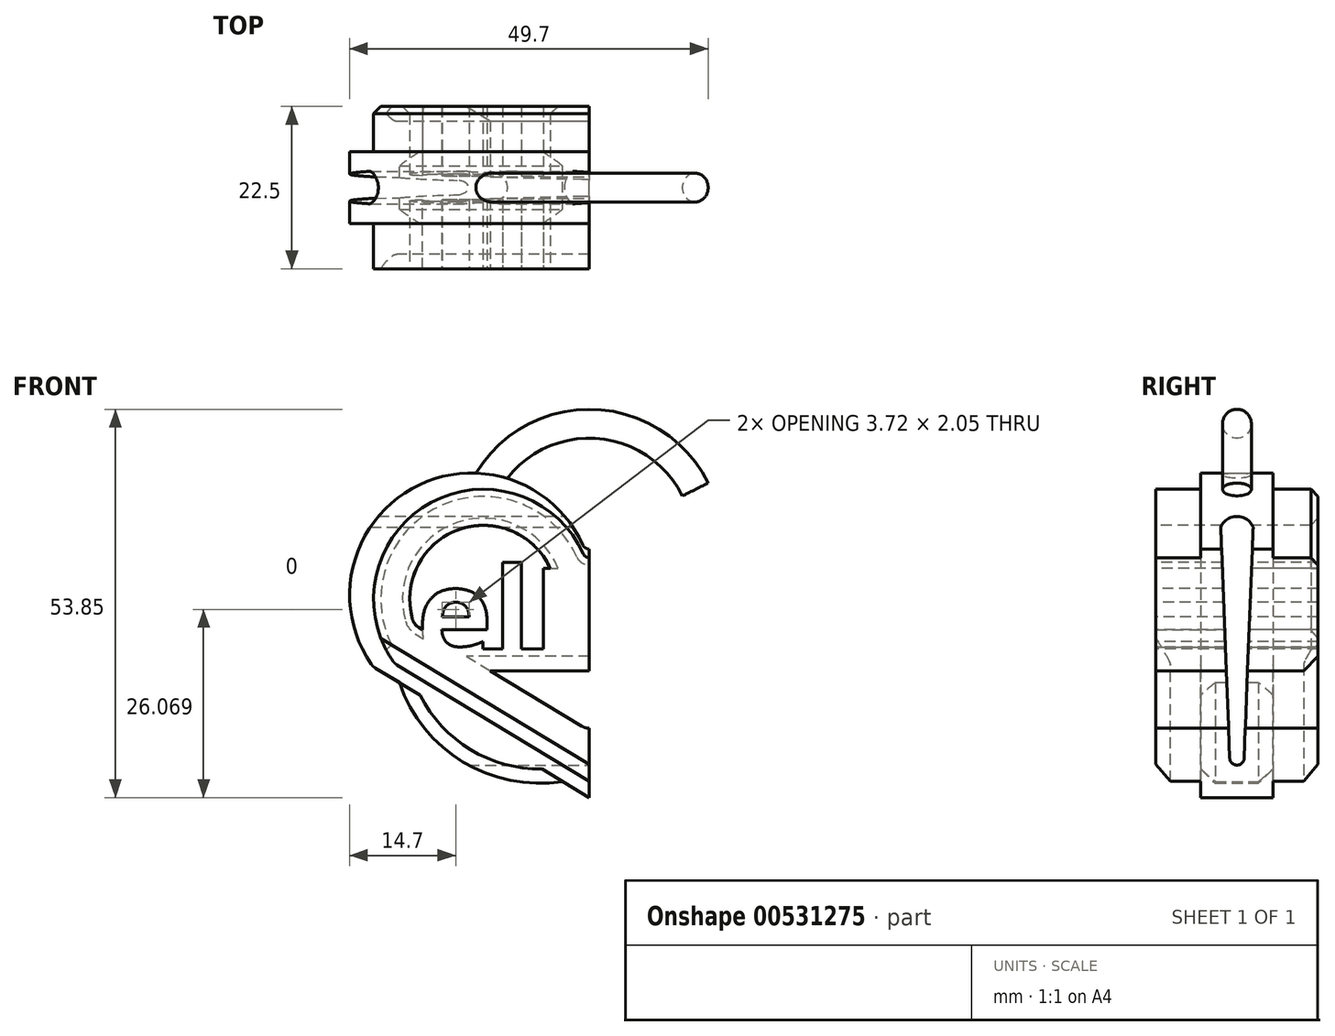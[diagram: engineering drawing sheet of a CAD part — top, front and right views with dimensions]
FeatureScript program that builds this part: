
annotation { "Feature Type Name" : "Feature", "Feature Type Description" : "" }
export const myFeature = defineFeature(function(context is Context, id is Id, definition is map)
    precondition{}
    {
        {
            var Q0;
            Q0=qCreatedBy(makeId("Front.planeOp"),FACE);
            var sketch = newSketch(context, id + "F0", { "sketchPlane" : qUnion([Q0])});
            skLineSegment(sketch, "E0", {"start": v(0, 22.5) * mm, "end": v(0, -22.5) * mm});
            skArc(sketch, "E1", {"start": v(-0.91, 12.55) * mm, "mid": v(-24.6, 20.33) * mm, "end": v(-30.26, -3.96) * mm});
            skPoint(sketch, "E2", {"position": v(-16.32, 22.5) * mm});
            skLineSegment(sketch, "E3", {"start": v(-29.64, -4.54) * mm, "end": v(0, -22.5) * mm});
            skLineSegment(sketch, "E4", {"start": v(0, 0) * mm, "end": v(-45, 0) * mm, "construction": true});
            skPoint(sketch, "E5", {"position": v(-22.5, 0) * mm});
            skArc(sketch, "E6", {"start": v(-26.32, -6.55) * mm, "mid": v(-17.5, -17.55) * mm, "end": v(-3.68, -20.27) * mm});
            skLineSegment(sketch, "E7.MirrorCS", {"start": v(29.64, -4.54) * mm, "end": v(0, -22.5) * mm});
            skArc(sketch, "E8.MirrorCS", {"start": v(26.32, -6.55) * mm, "mid": v(17.5, -17.55) * mm, "end": v(3.68, -20.27) * mm});
            skPoint(sketch, "E9.MirrorP", {"position": v(22.5, 0) * mm});
            skArc(sketch, "E10.MirrorCS", {"start": v(0.91, 12.55) * mm, "mid": v(24.6, 20.33) * mm, "end": v(30.26, -3.96) * mm});
            skPoint(sketch, "E11.visualSharp", {"position": v(0, 10) * mm});
            skArc(sketch, "E11.filletArc", {"start": v(-0.91, 12.55) * mm, "mid": v(0, 11.96) * mm, "end": v(0.91, 12.55) * mm});
            skPoint(sketch, "E12.visualSharp", {"position": v(-30, -4.32) * mm});
            skArc(sketch, "E12.filletArc", {"start": v(-30.26, -3.96) * mm, "mid": v(-29.98, -4.28) * mm, "end": v(-29.64, -4.54) * mm});
            skPoint(sketch, "E13.visualSharp", {"position": v(30, -4.32) * mm});
            skArc(sketch, "E13.filletArc", {"start": v(29.64, -4.54) * mm, "mid": v(29.98, -4.28) * mm, "end": v(30.26, -3.96) * mm});
            skSolve(sketch);
        }
        {
            var Q0;
            {var subQ0=sQuery(id+"F0.wireOp",EDGE,"E6");Q0=makeQuery(id+"F0.imprint","IMPRINT",FACE,{"disambiguationData":[TD([[makeQuery(id+"F0.imprint","IMPRINT",EDGE,{"derivedFrom":subQ0}),1.0]])]});}
            var Q1;
            {var subQ5=sQuery(id+"F0.wireOp",EDGE,"E1");Q1=makeQuery(id+"F0.imprint","IMPRINT",FACE,{"disambiguationData":[TD([[makeQuery(id+"F0.imprint","IMPRINT",EDGE,{"derivedFrom":subQ5}),1.0]])]});}
            var Q2;
            {var subQ9=sQuery(id+"F0.wireOp",EDGE,"E10.MirrorCS");Q2=makeQuery(id+"F0.imprint","IMPRINT",FACE,{"disambiguationData":[TD([[makeQuery(id+"F0.imprint","IMPRINT",EDGE,{"derivedFrom":subQ9}),-1.0]])]});}
            var Q3;
            {var subQ0=sQuery(id+"F0.wireOp",EDGE,"E8.MirrorCS");Q3=makeQuery(id+"F0.imprint","IMPRINT",FACE,{"disambiguationData":[TD([[makeQuery(id+"F0.imprint","IMPRINT",EDGE,{"derivedFrom":subQ0}),-1.0]])]});}
            extrude(context, id + "F1", {"entities" : qUnion([Q0, Q1, Q2, Q3]), "endBound" : BoundingType.SYMMETRIC, "depth" : 10 * mm, "offsetDistance" : 25 * mm});
        }
        {
            var Q0;
            {var subQ5=sQuery(id+"F0.wireOp",EDGE,"E1");Q0=makeQuery(id+"F0.imprint","IMPRINT",FACE,{"disambiguationData":[TD([[makeQuery(id+"F0.imprint","IMPRINT",EDGE,{"derivedFrom":subQ5}),1.0]])]});}
            var Q1;
            {var subQ9=sQuery(id+"F0.wireOp",EDGE,"E10.MirrorCS");Q1=makeQuery(id+"F0.imprint","IMPRINT",FACE,{"disambiguationData":[TD([[makeQuery(id+"F0.imprint","IMPRINT",EDGE,{"derivedFrom":subQ9}),-1.0]])]});}
            extrude(context, id + "F2", {"entities" : qUnion([Q0, Q1]), "endBound" : BoundingType.SYMMETRIC, "depth" : 25 * mm, "offsetDistance" : 25 * mm});
        }
        {
            var Q0;
            Q0=makeQuery(id+"F2.opExtrude","SWEPT_BODY",BODY,{"disambiguationData":[OSD([sQuery(id+"F0.wireOp",EDGE,"E1"),sQuery(id+"F0.wireOp",EDGE,"E3"),sQuery(id+"F0.wireOp",EDGE,"E7.MirrorCS"),sQuery(id+"F0.wireOp",EDGE,"E10.MirrorCS"),sQuery(id+"F0.wireOp",EDGE,"E11.filletArc"),sQuery(id+"F0.wireOp",EDGE,"E12.filletArc"),sQuery(id+"F0.wireOp",EDGE,"E13.filletArc")])]});
            var Q1;
            Q1=qCreatedBy(makeId("Origin.pointOp"),VERTEX);
            transform(context, id + "F3", {"entities" : qUnion([Q0]), "transformType" : TransformType.SCALE_UNIFORMLY, "scale" : .9, "scalePoint" : qUnion([Q1]), "makeCopy" : false});
        }
        {
            var Q0;
            Q0=makeQuery(id+"F1.opExtrude","CAP_EDGE",EDGE,{"disambiguationData":[OSD([sQuery(id+"F0.wireOp",EDGE,"E8.MirrorCS")])],"isStart":false});
            var Q1;
            Q1=makeQuery(id+"F1.opExtrude","CAP_EDGE",EDGE,{"disambiguationData":[OSD([sQuery(id+"F0.wireOp",EDGE,"E8.MirrorCS")])],"isStart":true});
            var Q2;
            Q2=makeQuery(id+"F2.opExtrude","CAP_EDGE",EDGE,{"disambiguationData":[OSD([sQuery(id+"F0.wireOp",EDGE,"E7.MirrorCS")])],"isStart":false});
            var Q3;
            Q3=makeQuery(id+"F2.opExtrude","CAP_EDGE",EDGE,{"disambiguationData":[OSD([sQuery(id+"F0.wireOp",EDGE,"E13.filletArc")])],"isStart":false});
            var Q4;
            Q4=makeQuery(id+"F2.opExtrude","CAP_EDGE",EDGE,{"disambiguationData":[OSD([sQuery(id+"F0.wireOp",EDGE,"E7.MirrorCS")])],"isStart":true});
            var Q5;
            Q5=makeQuery(id+"F2.opExtrude","CAP_EDGE",EDGE,{"disambiguationData":[OSD([sQuery(id+"F0.wireOp",EDGE,"E3")])],"isStart":false});
            var Q6;
            Q6=makeQuery(id+"F1.opExtrude","CAP_EDGE",EDGE,{"disambiguationData":[OSD([sQuery(id+"F0.wireOp",EDGE,"E6")])],"isStart":false});
            var Q7;
            Q7=makeQuery(id+"F1.opExtrude","CAP_EDGE",EDGE,{"disambiguationData":[OSD([sQuery(id+"F0.wireOp",EDGE,"E6")])],"isStart":true});
            var Q8;
            Q8=makeQuery(id+"F2.opExtrude","CAP_EDGE",EDGE,{"disambiguationData":[OSD([sQuery(id+"F0.wireOp",EDGE,"E3")])],"isStart":true});
            chamfer(context, id + "F4", {"entities" : qUnion([Q0, Q1, Q2, Q3, Q4, Q5, Q6, Q7, Q8]), "width" : 2 * mm});
        }
        {
            var Q0;
            Q0=makeQuery(id+"F1.opExtrude","SWEPT_FACE",FACE,{"disambiguationData":[OSD([sQuery(id+"F0.wireOp",EDGE,"E10.MirrorCS")])]});
            var Q1;
            Q1=makeQuery(id+"F2.opExtrude","CAP_EDGE",EDGE,{"disambiguationData":[OSD([sQuery(id+"F0.wireOp",EDGE,"E1")])],"isStart":true});
            var Q2;
            Q2=makeQuery(id+"F2.opExtrude","CAP_EDGE",EDGE,{"disambiguationData":[OSD([sQuery(id+"F0.wireOp",EDGE,"E10.MirrorCS")])],"isStart":false});
            chamfer(context, id + "F5", {"entities" : qUnion([Q0, Q1, Q2]), "width" : 1 * mm, "tangentPropagation" : true});
        }
        {
            var Q0;
            Q0=qCreatedBy(makeId("Right.planeOp"),FACE);
            var sketch = newSketch(context, id + "F6", { "sketchPlane" : qUnion([Q0])});
            skLineSegment(sketch, "E14", {"start": v(15, 15) * mm, "end": v(-15, 15) * mm, "construction": true});
            skLineSegment(sketch, "E15", {"start": v(-4, 22.5) * mm, "end": v(4, 22.5) * mm, "construction": true});
            skLineSegment(sketch, "E16.0", {"start": v(-5, -22.5) * mm, "end": v(5, -22.5) * mm, "construction": true});
            skLineSegment(sketch, "E17.0", {"start": v(11.25, -17.91) * mm, "end": v(11.25, -1.3) * mm, "construction": true});
            skLineSegment(sketch, "E18.0", {"start": v(11.25, -1.3) * mm, "end": v(11.25, 19.25) * mm, "construction": true});
            skLineSegment(sketch, "E19.0", {"start": v(-11.25, 19.25) * mm, "end": v(-11.25, -1.3) * mm, "construction": true});
            skLineSegment(sketch, "E20.0", {"start": v(-11.25, -1.3) * mm, "end": v(-11.25, -17.91) * mm, "construction": true});
            skLineSegment(sketch, "E21.0", {"start": v(-3, -6.55) * mm, "end": v(3, -6.55) * mm, "construction": true});
            skArc(sketch, "E22", {"start": v(2.25, 15) * mm, "mid": v(0, 16.5) * mm, "end": v(-2.25, 15) * mm});
            skPoint(sketch, "E23", {"position": v(0, 16.5) * mm});
            skPoint(sketch, "E24", {"position": v(0, 22.5) * mm});
            skPoint(sketch, "E25", {"position": v(0, 15) * mm});
            skLineSegment(sketch, "E26", {"start": v(15, -42.64) * mm, "end": v(-15, -42.64) * mm, "construction": true});
            skPoint(sketch, "E27", {"position": v(0, -42.64) * mm});
            skLineSegment(sketch, "E28", {"start": v(2.25, 15) * mm, "end": v(1, -17.04) * mm});
            skLineSegment(sketch, "E29", {"start": v(-2.25, 15) * mm, "end": v(-1, -17.04) * mm});
            skArc(sketch, "E30.filletArc", {"start": v(-1, -17.04) * mm, "mid": v(0, -18) * mm, "end": v(1, -17.04) * mm});
            skSolve(sketch);
        }
        {
            var Q0;
            Q0 = qSketchRegion(id + "F6", true);
            extrude(context, id + "F7", {"entities" : qUnion([Q0]), "operationType" : NewBodyOperationType.REMOVE, "endBound" : BoundingType.SYMMETRIC, "oppositeDirection" : true, "depth" : 70 * mm, "offsetDistance" : 25 * mm, "hasSecondDirection" : true, "secondDirectionBound" : SecondDirectionBoundingType.THROUGH_ALL, "secondDirectionOppositeDirection" : true, "secondDirectionDepth" : 25 * mm});
        }
        {
            var Q0;
            Q0=makeQuery(id+"F2.opExtrude","CAP_FACE",FACE,{"disambiguationData":[OSD([sQuery(id+"F0.wireOp",EDGE,"E1"),sQuery(id+"F0.wireOp",EDGE,"E3"),sQuery(id+"F0.wireOp",EDGE,"E7.MirrorCS"),sQuery(id+"F0.wireOp",EDGE,"E10.MirrorCS"),sQuery(id+"F0.wireOp",EDGE,"E11.filletArc"),sQuery(id+"F0.wireOp",EDGE,"E12.filletArc"),sQuery(id+"F0.wireOp",EDGE,"E13.filletArc")])],"isStart":false});
            var sketch = newSketch(context, id + "F8", { "sketchPlane" : qUnion([Q0])});
            skArc(sketch, "E31.0", {"start": v(-5.38, 9.24) * mm, "mid": v(-18.2, 14.63) * mm, "end": v(-24.5, 2.24) * mm});
            skArc(sketch, "E31.1", {"start": v(5.38, 9.24) * mm, "mid": v(0, 5.76) * mm, "end": v(-5.38, 9.24) * mm});
            skLineSegment(sketch, "E31.2", {"start": v(-23.62, 1.08) * mm, "end": v(-1.04, -12.6) * mm});
            skLineSegment(sketch, "E31.3", {"start": v(1.04, -12.6) * mm, "end": v(23.62, 1.08) * mm});
            skArc(sketch, "E31.4", {"start": v(24.5, 2.24) * mm, "mid": v(18.2, 14.63) * mm, "end": v(5.38, 9.24) * mm});
            skPoint(sketch, "E32.visualSharp", {"position": v(0, -13.23) * mm});
            skArc(sketch, "E32.filletArc", {"start": v(-1.04, -12.6) * mm, "mid": v(0, -12.9) * mm, "end": v(1.04, -12.6) * mm});
            skPoint(sketch, "E33.visualSharp", {"position": v(-24.25, 1.46) * mm});
            skArc(sketch, "E33.filletArc", {"start": v(-24.5, 2.24) * mm, "mid": v(-24.17, 1.58) * mm, "end": v(-23.62, 1.08) * mm});
            skPoint(sketch, "E34.visualSharp", {"position": v(24.25, 1.46) * mm});
            skArc(sketch, "E34.filletArc", {"start": v(23.62, 1.08) * mm, "mid": v(24.17, 1.58) * mm, "end": v(24.5, 2.24) * mm});
            skText(sketch, "E35", { "text": "elLex", "fontName": "OpenSans-Bold.ttf"});
            skLineSegment(sketch, "E36.bottom", {"start": v(-23.92, -1.91) * mm, "end": v(23.92, -1.91) * mm});
            skLineSegment(sketch, "E36.top", {"start": v(-21.45, -4.91) * mm, "end": v(21.45, -4.91) * mm});
            skLineSegment(sketch, "E36.left", {"start": v(-23.92, -1.91) * mm, "end": v(-23.92, -3.41) * mm});
            skLineSegment(sketch, "E36.right", {"start": v(23.92, -1.91) * mm, "end": v(23.92, -3.41) * mm});
            skLineSegment(sketch, "E37.0", {"start": v(-27.4, -1.3) * mm, "end": v(0, -17.91) * mm, "construction": true});
            skLineSegment(sketch, "E38.0", {"start": v(0, -17.91) * mm, "end": v(27.4, -1.3) * mm, "construction": true});
            skPoint(sketch, "E39.orphan", {"position": v(-23.92, -4.91) * mm});
            skPoint(sketch, "E40.orphan", {"position": v(23.92, -4.91) * mm});
            skLineSegment(sketch, "E41.bottom", {"start": v(-23.05, 10.9) * mm, "end": v(-1.78, 10.9) * mm});
            skLineSegment(sketch, "E41.top", {"start": v(-23.92, 7.9) * mm, "end": v(23.92, 7.9) * mm});
            skLineSegment(sketch, "E41.left", {"start": v(-23.92, 9.4) * mm, "end": v(-23.92, 7.9) * mm});
            skLineSegment(sketch, "E41.right", {"start": v(23.92, 9.4) * mm, "end": v(23.92, 7.9) * mm});
            skArc(sketch, "E42.0", {"start": v(1.73, 10.88) * mm, "mid": v(0, 9.76) * mm, "end": v(-1.73, 10.88) * mm});
            skLineSegment(sketch, "E43", {"start": v(1.73, 10.9) * mm, "end": v(23.05, 10.9) * mm});
            skPoint(sketch, "E44.orphan", {"position": v(-23.92, 10.9) * mm});
            const initialGuessF8  = {"E35": [-0.02392, -0.00341, 1, 0, 0.0128]};
            skSetInitialGuess(sketch, initialGuessF8);
            skSolve(sketch);
        }
        {
            var Q0;
            {var subQ13=sQuery(id+"F8.wireOp",EDGE,"E31.4");Q0=makeQuery(id+"F8.imprint","IMPRINT",FACE,{"disambiguationData":[TD([[makeQuery(id+"F8.imprint","IMPRINT",EDGE,{"derivedFrom":subQ13}),1.0]])]});}
            var Q1;
            Q1=makeQuery(id+"F8.imprint","IMPRINT",FACE,{"disambiguationData":[TD([[makeQuery(id+"F8.imprint","IMPRINT",EDGE,{"derivedFrom":sQuery(id+"F8.wireOp",EDGE,"E35.sketch_text.stroke-30")}),1.0]])]});
            var Q2;
            Q2=makeQuery(id+"F8.imprint","IMPRINT",FACE,{"disambiguationData":[TD([[makeQuery(id+"F8.imprint","IMPRINT",EDGE,{"derivedFrom":sQuery(id+"F8.wireOp",EDGE,"E35.sketch_text.stroke-0")}),1.0]])]});
            var Q3;
            {var subQ4=sQuery(id+"F8.wireOp",EDGE,"E33.filletArc");Q3=makeQuery(id+"F8.imprint","IMPRINT",FACE,{"disambiguationData":[TD([[makeQuery(id+"F8.imprint","IMPRINT",EDGE,{"derivedFrom":subQ4}),1.0]])]});}
            var Q4;
            {var subQ0=sQuery(id+"F8.wireOp",EDGE,"E41.top");var subQ1=sQuery(id+"F8.wireOp",EDGE,"E35.sketch_text.stroke-23");var subQ2=makeQuery(id+"F8.imprint","INTERSECT",VERTEX,{"derivedFrom":[subQ1,subQ0]});Q4=makeQuery(id+"F8.imprint","IMPRINT",FACE,{"disambiguationData":[TD([[makeQuery(id+"F8.imprint","IMPRINT",EDGE,{"disambiguationData":[TD([[subQ2,-1.0]])],"derivedFrom":subQ1}),1.0]])]});}
            var Q5;
            {var subQ2=sQuery(id+"F8.wireOp",EDGE,"E34.filletArc");Q5=makeQuery(id+"F8.imprint","IMPRINT",FACE,{"disambiguationData":[TD([[makeQuery(id+"F8.imprint","IMPRINT",EDGE,{"derivedFrom":subQ2}),1.0]])]});}
            var Q6;
            {var subQ11=sQuery(id+"F8.wireOp",EDGE,"E35.sketch_text.stroke-22");Q6=makeQuery(id+"F8.imprint","IMPRINT",FACE,{"disambiguationData":[TD([[makeQuery(id+"F8.imprint","IMPRINT",EDGE,{"derivedFrom":subQ11}),1.0]])]});}
            var Q7;
            {var subQ0=sQuery(id+"F8.wireOp",EDGE,"E41.bottom");var subQ1=sQuery(id+"F8.wireOp",EDGE,"E31.0");var subQ2=makeQuery(id+"F8.imprint","INTERSECT",VERTEX,{"disambiguationData":[OD(0.0)],"derivedFrom":[subQ1,subQ0]});Q7=makeQuery(id+"F8.imprint","IMPRINT",FACE,{"disambiguationData":[TD([[makeQuery(id+"F8.imprint","IMPRINT",EDGE,{"disambiguationData":[TD([[subQ2,1.0]])],"derivedFrom":subQ1}),1.0]])]});}
            var Q8;
            {var subQ0=sQuery(id+"F8.wireOp",EDGE,"E43");var subQ1=sQuery(id+"F8.wireOp",EDGE,"E31.4");var subQ2=makeQuery(id+"F8.imprint","INTERSECT",VERTEX,{"disambiguationData":[OD(0.0)],"derivedFrom":[subQ1,subQ0]});Q8=makeQuery(id+"F8.imprint","IMPRINT",FACE,{"disambiguationData":[TD([[makeQuery(id+"F8.imprint","IMPRINT",EDGE,{"disambiguationData":[TD([[subQ2,-1.0]])],"derivedFrom":subQ1}),1.0]])]});}
            var Q9;
            {var subQ0=sQuery(id+"F8.wireOp",EDGE,"E36.bottom");var subQ1=sQuery(id+"F8.wireOp",EDGE,"E31.3");var subQ2=makeQuery(id+"F8.imprint","INTERSECT",VERTEX,{"derivedFrom":[subQ1,subQ0]});Q9=makeQuery(id+"F8.imprint","IMPRINT",FACE,{"disambiguationData":[TD([[makeQuery(id+"F8.imprint","IMPRINT",EDGE,{"disambiguationData":[TD([[subQ2,-1.0]])],"derivedFrom":subQ1}),1.0]])]});}
            var Q10;
            {var subQ0=sQuery(id+"F8.wireOp",EDGE,"E32.filletArc");Q10=makeQuery(id+"F8.imprint","IMPRINT",FACE,{"disambiguationData":[TD([[makeQuery(id+"F8.imprint","IMPRINT",EDGE,{"derivedFrom":subQ0}),1.0]])]});}
            extrude(context, id + "F9", {"entities" : qUnion([Q0, Q1, Q2, Q3, Q4, Q5, Q6, Q7, Q8, Q9, Q10]), "operationType" : NewBodyOperationType.REMOVE, "endBound" : BoundingType.THROUGH_ALL, "oppositeDirection" : true, "depth" : 25 * mm, "offsetDistance" : 25 * mm});
        }
        {
            var Q0;
            Q0=makeQuery(id+"F9.boolean.opBoolean","COPY",EDGE,{"derivedFrom":makeQuery(id+"F9.opExtrude","CAP_EDGE",EDGE,{"disambiguationData":[OSD([sQuery(id+"F8.wireOp",EDGE,"E36.top")])],"isStart":true})});
            var Q1;
            {var subQ0=sQuery(id+"F8.wireOp",EDGE,"E31.2");Q1=makeQuery(id+"F9.boolean.opBoolean","COPY",EDGE,{"derivedFrom":makeQuery(id+"F9.opExtrude","CAP_EDGE",EDGE,{"disambiguationData":[OSD([subQ0]),TDD([makeQuery(id+"F8.imprint","IMPRINT",EDGE,{"disambiguationData":[TD([[makeQuery(id+"F8.imprint","INTERSECT",VERTEX,{"derivedFrom":[subQ0,sQuery(id+"F8.wireOp",EDGE,"E32.filletArc")]}),1.0]])],"derivedFrom":subQ0})])],"isStart":true})});}
            var Q2;
            Q2=makeQuery(id+"F9.boolean.opBoolean","INTERSECT",EDGE,{"derivedFrom":[makeQuery(id+"F2.opExtrude","CAP_FACE",FACE,{"disambiguationData":[OSD([sQuery(id+"F0.wireOp",EDGE,"E1"),sQuery(id+"F0.wireOp",EDGE,"E3"),sQuery(id+"F0.wireOp",EDGE,"E7.MirrorCS"),sQuery(id+"F0.wireOp",EDGE,"E10.MirrorCS"),sQuery(id+"F0.wireOp",EDGE,"E11.filletArc"),sQuery(id+"F0.wireOp",EDGE,"E12.filletArc"),sQuery(id+"F0.wireOp",EDGE,"E13.filletArc")])],"isStart":true}),makeQuery(id+"F9.opExtrude","SWEPT_FACE",FACE,{"disambiguationData":[OSD([sQuery(id+"F8.wireOp",EDGE,"E36.top")])]})]});
            var Q3;
            {var subQ0=sQuery(id+"F8.wireOp",EDGE,"E31.3");Q3=makeQuery(id+"F9.boolean.opBoolean","INTERSECT",EDGE,{"derivedFrom":[makeQuery(id+"F2.opExtrude","CAP_FACE",FACE,{"disambiguationData":[OSD([sQuery(id+"F0.wireOp",EDGE,"E1"),sQuery(id+"F0.wireOp",EDGE,"E3"),sQuery(id+"F0.wireOp",EDGE,"E7.MirrorCS"),sQuery(id+"F0.wireOp",EDGE,"E10.MirrorCS"),sQuery(id+"F0.wireOp",EDGE,"E11.filletArc"),sQuery(id+"F0.wireOp",EDGE,"E12.filletArc"),sQuery(id+"F0.wireOp",EDGE,"E13.filletArc")])],"isStart":true}),makeQuery(id+"F9.opExtrude","SWEPT_FACE",FACE,{"disambiguationData":[OSD([subQ0]),TDD([makeQuery(id+"F8.imprint","IMPRINT",EDGE,{"disambiguationData":[TD([[makeQuery(id+"F8.imprint","INTERSECT",VERTEX,{"derivedFrom":[subQ0,sQuery(id+"F8.wireOp",EDGE,"E32.filletArc")]}),-1.0]])],"derivedFrom":subQ0})])]})]});}
            chamfer(context, id + "F10", {"entities" : qUnion([Q0, Q1, Q2, Q3]), "width" : 2 * mm, "tangentPropagation" : true});
        }
        {
            var Q0;
            Q0=makeQuery(id+"F9.boolean.opBoolean","COPY",EDGE,{"derivedFrom":makeQuery(id+"F9.opExtrude","CAP_EDGE",EDGE,{"disambiguationData":[OSD([sQuery(id+"F8.wireOp",EDGE,"E31.0")])],"isStart":true})});
            var Q1;
            Q1=makeQuery(id+"F9.boolean.opBoolean","COPY",EDGE,{"derivedFrom":makeQuery(id+"F9.opExtrude","CAP_EDGE",EDGE,{"disambiguationData":[OSD([sQuery(id+"F8.wireOp",EDGE,"E31.4")])],"isStart":true})});
            var Q2;
            Q2=makeQuery(id+"F9.boolean.opBoolean","INTERSECT",EDGE,{"derivedFrom":[makeQuery(id+"F2.opExtrude","CAP_FACE",FACE,{"disambiguationData":[OSD([sQuery(id+"F0.wireOp",EDGE,"E1"),sQuery(id+"F0.wireOp",EDGE,"E3"),sQuery(id+"F0.wireOp",EDGE,"E7.MirrorCS"),sQuery(id+"F0.wireOp",EDGE,"E10.MirrorCS"),sQuery(id+"F0.wireOp",EDGE,"E11.filletArc"),sQuery(id+"F0.wireOp",EDGE,"E12.filletArc"),sQuery(id+"F0.wireOp",EDGE,"E13.filletArc")])],"isStart":true}),makeQuery(id+"F9.opExtrude","SWEPT_FACE",FACE,{"disambiguationData":[OSD([sQuery(id+"F8.wireOp",EDGE,"E31.1")])]})]});
            var Q3;
            Q3=makeQuery(id+"F9.boolean.opBoolean","INTERSECT",EDGE,{"derivedFrom":[makeQuery(id+"F2.opExtrude","CAP_FACE",FACE,{"disambiguationData":[OSD([sQuery(id+"F0.wireOp",EDGE,"E1"),sQuery(id+"F0.wireOp",EDGE,"E3"),sQuery(id+"F0.wireOp",EDGE,"E7.MirrorCS"),sQuery(id+"F0.wireOp",EDGE,"E10.MirrorCS"),sQuery(id+"F0.wireOp",EDGE,"E11.filletArc"),sQuery(id+"F0.wireOp",EDGE,"E12.filletArc"),sQuery(id+"F0.wireOp",EDGE,"E13.filletArc")])],"isStart":true}),makeQuery(id+"F9.opExtrude","SWEPT_FACE",FACE,{"disambiguationData":[OSD([sQuery(id+"F8.wireOp",EDGE,"E31.0")])]})]});
            var Q4;
            Q4=makeQuery(id+"F7.boolean.opBoolean","INTERSECT",EDGE,{"disambiguationData":[OD(1.0)],"derivedFrom":[makeQuery(id+"F1.opExtrude","SWEPT_FACE",FACE,{"disambiguationData":[OSD([sQuery(id+"F0.wireOp",EDGE,"E10.MirrorCS")])]}),makeQuery(id+"F7.opExtrude","SWEPT_FACE",FACE,{"disambiguationData":[OSD([sQuery(id+"F6.wireOp",EDGE,"E22")])]})]});
            var Q5;
            Q5=makeQuery(id+"F7.boolean.opBoolean","INTERSECT",EDGE,{"derivedFrom":[makeQuery(id+"F1.opExtrude","SWEPT_FACE",FACE,{"disambiguationData":[OSD([sQuery(id+"F0.wireOp",EDGE,"E8.MirrorCS")])]}),makeQuery(id+"F7.opExtrude","SWEPT_FACE",FACE,{"disambiguationData":[OSD([sQuery(id+"F6.wireOp",EDGE,"E30.filletArc")])]})]});
            var Q6;
            Q6=makeQuery(id+"F7.boolean.opBoolean","INTERSECT",EDGE,{"disambiguationData":[OD(1.0)],"derivedFrom":[makeQuery(id+"F1.opExtrude","SWEPT_FACE",FACE,{"disambiguationData":[OSD([sQuery(id+"F0.wireOp",EDGE,"E10.MirrorCS")])]}),makeQuery(id+"F7.opExtrude","SWEPT_FACE",FACE,{"disambiguationData":[OSD([sQuery(id+"F6.wireOp",EDGE,"E29")])]})]});
            var Q7;
            Q7=makeQuery(id+"F7.boolean.opBoolean","INTERSECT",EDGE,{"disambiguationData":[OD(1.0)],"derivedFrom":[makeQuery(id+"F1.opExtrude","SWEPT_FACE",FACE,{"disambiguationData":[OSD([sQuery(id+"F0.wireOp",EDGE,"E10.MirrorCS")])]}),makeQuery(id+"F7.opExtrude","SWEPT_FACE",FACE,{"disambiguationData":[OSD([sQuery(id+"F6.wireOp",EDGE,"E28")])]})]});
            var Q8;
            Q8=makeQuery(id+"F7.boolean.opBoolean","INTERSECT",EDGE,{"disambiguationData":[OD(1.0)],"derivedFrom":[makeQuery(id+"F1.opExtrude","SWEPT_FACE",FACE,{"disambiguationData":[OSD([sQuery(id+"F0.wireOp",EDGE,"E1")])]}),makeQuery(id+"F7.opExtrude","SWEPT_FACE",FACE,{"disambiguationData":[OSD([sQuery(id+"F6.wireOp",EDGE,"E22")])]})]});
            var Q9;
            Q9=makeQuery(id+"F7.boolean.opBoolean","INTERSECT",EDGE,{"derivedFrom":[makeQuery(id+"F1.opExtrude","SWEPT_FACE",FACE,{"disambiguationData":[OSD([sQuery(id+"F0.wireOp",EDGE,"E6")])]}),makeQuery(id+"F7.opExtrude","SWEPT_FACE",FACE,{"disambiguationData":[OSD([sQuery(id+"F6.wireOp",EDGE,"E30.filletArc")])]})]});
            var Q10;
            Q10=makeQuery(id+"F7.boolean.opBoolean","INTERSECT",EDGE,{"disambiguationData":[OD(1.0)],"derivedFrom":[makeQuery(id+"F1.opExtrude","SWEPT_FACE",FACE,{"disambiguationData":[OSD([sQuery(id+"F0.wireOp",EDGE,"E1")])]}),makeQuery(id+"F7.opExtrude","SWEPT_FACE",FACE,{"disambiguationData":[OSD([sQuery(id+"F6.wireOp",EDGE,"E28")])]})]});
            var Q11;
            Q11=makeQuery(id+"F7.boolean.opBoolean","INTERSECT",EDGE,{"disambiguationData":[OD(1.0)],"derivedFrom":[makeQuery(id+"F1.opExtrude","SWEPT_FACE",FACE,{"disambiguationData":[OSD([sQuery(id+"F0.wireOp",EDGE,"E1")])]}),makeQuery(id+"F7.opExtrude","SWEPT_FACE",FACE,{"disambiguationData":[OSD([sQuery(id+"F6.wireOp",EDGE,"E29")])]})]});
            chamfer(context, id + "F11", {"entities" : qUnion([Q0, Q1, Q2, Q3, Q4, Q5, Q6, Q7, Q8, Q9, Q10, Q11]), "width" : 1 * mm, "tangentPropagation" : true});
        }
        {
            var Q0;
            Q0=qCreatedBy(makeId("Front.planeOp"),FACE);
            var sketch = newSketch(context, id + "F12", { "sketchPlane" : qUnion([Q0])});
            skArc(sketch, "E45.0", {"start": v(-30.26, -3.96) * mm, "mid": v(-24.6, 20.33) * mm, "end": v(-0.91, 12.55) * mm, "construction": true});
            skArc(sketch, "E46.0", {"start": v(0.91, 12.55) * mm, "mid": v(24.6, 20.33) * mm, "end": v(30.26, -3.96) * mm, "construction": true});
            skArc(sketch, "E47.0", {"start": v(-0.91, 12.55) * mm, "mid": v(0, 11.96) * mm, "end": v(0.91, 12.55) * mm, "construction": true});
            skArc(sketch, "E48.0", {"start": v(-5.4, 9.28) * mm, "mid": v(-18.22, 14.62) * mm, "end": v(-24.5, 2.24) * mm, "construction": true});
            skArc(sketch, "E49.0", {"start": v(24.5, 2.24) * mm, "mid": v(18.2, 14.63) * mm, "end": v(5.38, 9.24) * mm, "construction": true});
            skArc(sketch, "E50", {"start": v(14.69, 20.23) * mm, "mid": v(0, 29.35) * mm, "end": v(-14.69, 20.23) * mm});
            skSolve(sketch);
        }
        {
            var Q0;
            Q0=sQuery(id+"F12.wireOp",EDGE,"E50");
            var Q1;
            Q1=sQuery(id+"F12.wireOp",VERTEX,"E50.end");
            cPlane(context, id + "F13", {"entities" : qUnion([Q0, Q1]), "cplaneType" : CPlaneType.CURVE_POINT, "offset" : 25 * mm, "width" : 150 * mm, "height" : 150 * mm});
        }
        {
            var Q0;
            Q0=qCreatedBy(id+"F13.planeOp",FACE);
            var sketch = newSketch(context, id + "F14", { "sketchPlane" : qUnion([Q0])});
            skCircle(sketch, "E51", {"center": v(-22.14, 0) * mm, "radius": 2 * mm});
            skSolve(sketch);
        }
        {
            var Q0;
            Q0=makeQuery(id+"F14.imprint","IMPRINT",FACE,{"disambiguationData":[TD([[makeQuery(id+"F14.imprint","IMPRINT",EDGE,{"derivedFrom":sQuery(id+"F14.wireOp",EDGE,"E51")}),1.0]])]});
            var Q1;
            Q1=sQuery(id+"F12.wireOp",EDGE,"E50");
            sweep(context, id + "F15", {"operationType" : NewBodyOperationType.ADD, "profiles" : qUnion([Q0]), "path" : qUnion([Q1])});
        }
    });
